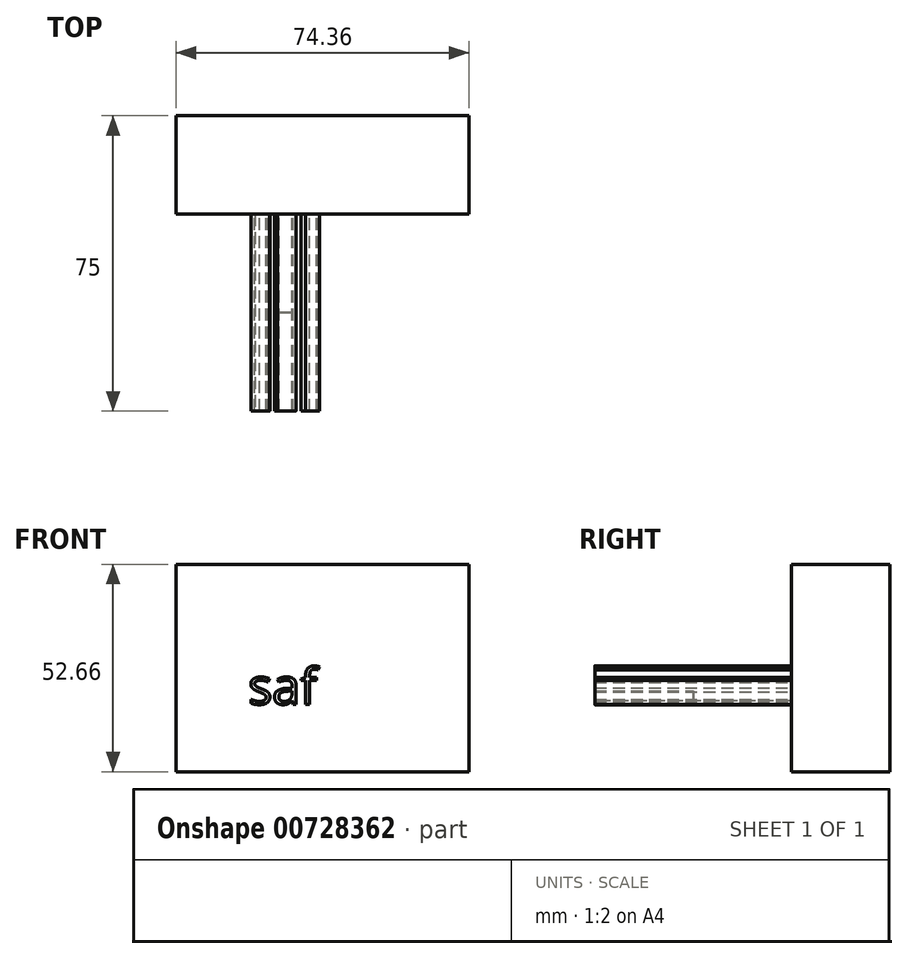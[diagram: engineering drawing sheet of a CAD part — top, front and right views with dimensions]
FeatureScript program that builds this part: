
annotation { "Feature Type Name" : "Feature", "Feature Type Description" : "" }
export const myFeature = defineFeature(function(context is Context, id is Id, definition is map)
    precondition{}
    {
        {
            var Q0;
            Q0=qCreatedBy(makeId("Front.planeOp"),FACE);
            var sketch = newSketch(context, id + "F0", { "sketchPlane" : qUnion([Q0])});
            skLineSegment(sketch, "E0.bottom", {"start": v(37.18, -26.33) * mm, "end": v(-37.18, -26.33) * mm});
            skLineSegment(sketch, "E0.top", {"start": v(37.18, 26.33) * mm, "end": v(-37.18, 26.33) * mm});
            skLineSegment(sketch, "E0.left", {"start": v(37.18, -26.33) * mm, "end": v(37.18, 26.33) * mm});
            skLineSegment(sketch, "E0.right", {"start": v(-37.18, -26.33) * mm, "end": v(-37.18, 26.33) * mm});
            skPoint(sketch, "E0.middle", {"position": v(0, 0) * mm});
            skSolve(sketch);
        }
        {
            var Q0;
            Q0=makeQuery(id+"F0.imprint","IMPRINT",FACE,{"disambiguationData":[TD([[makeQuery(id+"F0.imprint","IMPRINT",EDGE,{"derivedFrom":sQuery(id+"F0.wireOp",EDGE,"E0.bottom")}),-1.0]])]});
            extrude(context, id + "F1", {"entities" : qUnion([Q0]), "depth" : 25 * mm, "offsetDistance" : 25 * mm, "hasSecondDirection" : true, "secondDirectionOppositeDirection" : true, "secondDirectionDepth" : 25 * mm});
        }
        {
            var Q0;
            Q0=makeQuery(id+"F1.opExtrude","CAP_FACE",FACE,{"disambiguationData":[OSD([sQuery(id+"F0.wireOp",EDGE,"E0.bottom"),sQuery(id+"F0.wireOp",EDGE,"E0.top"),sQuery(id+"F0.wireOp",EDGE,"E0.left"),sQuery(id+"F0.wireOp",EDGE,"E0.right")])],"isStart":false});
            var sketch = newSketch(context, id + "F2", { "sketchPlane" : qUnion([Q0])});
            skText(sketch, "E1", { "text": "saf", "fontName": "OpenSans-Regular.ttf"});
            const initialGuessF2  = {"E1": [-0.01886, -0.00918, 1, 0, 0.00918]};
            skSetInitialGuess(sketch, initialGuessF2);
            skSolve(sketch);
        }
        {
            var Q0;
            Q0 = qSketchRegion(id + "F2", true);
            extrude(context, id + "F3", {"entities" : qUnion([Q0]), "operationType" : NewBodyOperationType.ADD, "depth" : 25 * mm, "offsetDistance" : 25 * mm});
        }
        {
            var Q0;
            {var subQ0=sQuery(id+"F0.wireOp",EDGE,"E0.left");var subQ1=sQuery(id+"F0.wireOp",EDGE,"E0.bottom");var subQ2=sQuery(id+"F0.wireOp",EDGE,"E0.right");var subQ3=sQuery(id+"F0.wireOp",EDGE,"E0.top");Q0=makeQuery(id+"F3.boolean.opBoolean","SPLIT",FACE,{"disambiguationData":[TD([makeQuery(id+"F1.opExtrude","SWEPT_FACE",FACE,{"disambiguationData":[OSD([subQ1])]})])],"derivedFrom":makeQuery(id+"F1.opExtrude","CAP_FACE",FACE,{"disambiguationData":[OSD([subQ1,subQ3,subQ0,subQ2])],"isStart":false})});}
            extrude(context, id + "F4", {"entities" : qUnion([Q0]), "operationType" : NewBodyOperationType.REMOVE, "oppositeDirection" : true, "depth" : 25 * mm, "offsetDistance" : 25 * mm});
        }
    });
